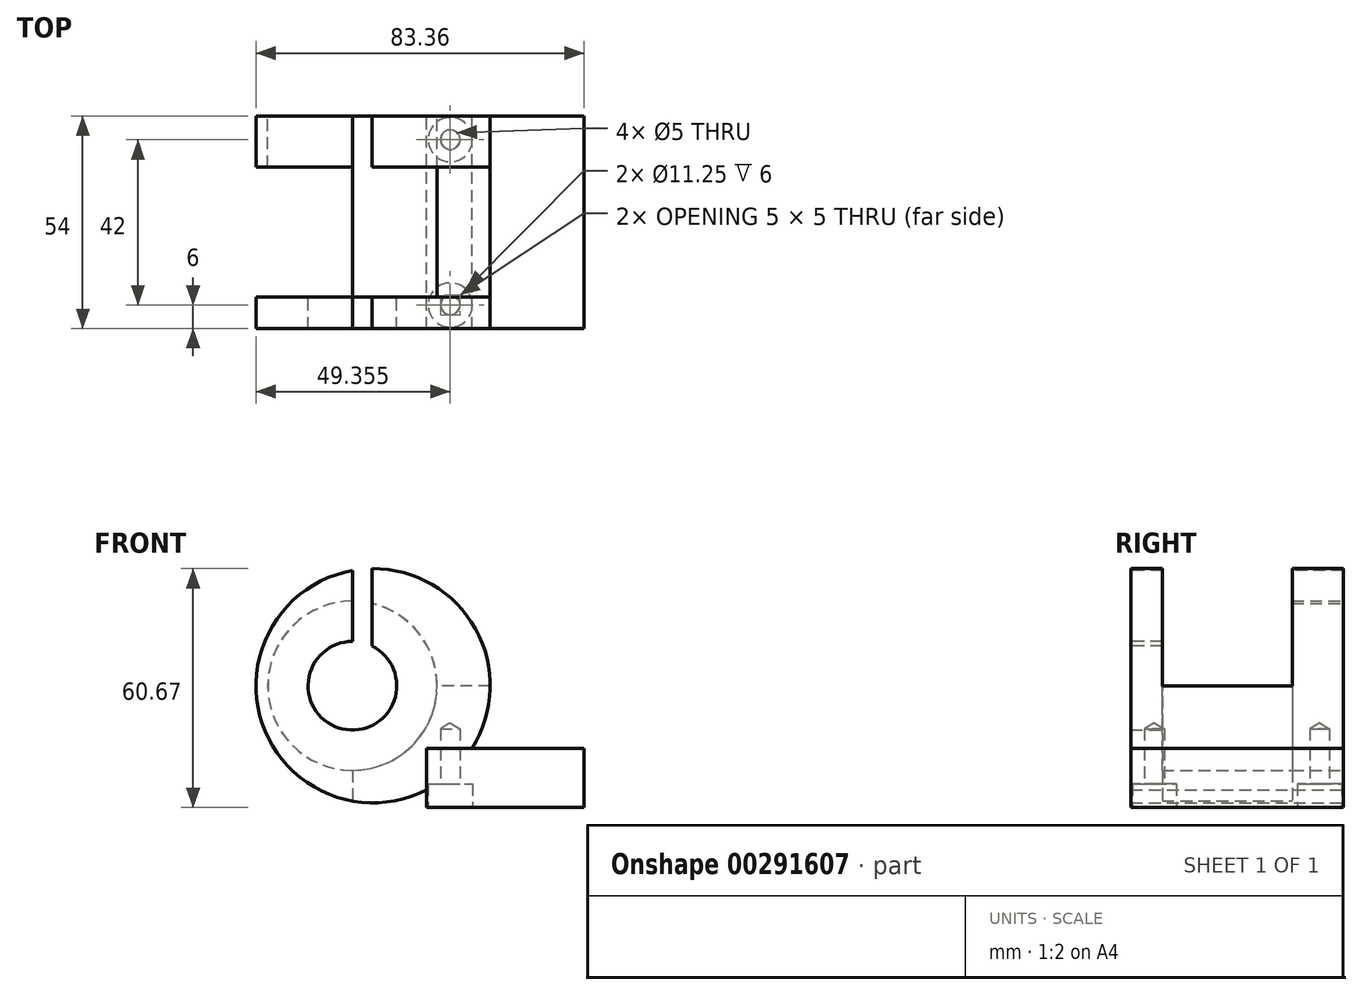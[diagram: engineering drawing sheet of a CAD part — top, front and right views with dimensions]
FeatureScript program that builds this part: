
annotation { "Feature Type Name" : "Feature", "Feature Type Description" : "" }
export const myFeature = defineFeature(function(context is Context, id is Id, definition is map)
    precondition{}
    {
        {
            var Q0;
            Q0=qCreatedBy(makeId("Front.planeOp"),FACE);
            var sketch = newSketch(context, id + "F0", { "sketchPlane" : qUnion([Q0])});
            skCircle(sketch, "E0", {"center": v(0, 0) * mm, "radius": 11.25 * mm});
            skCircle(sketch, "E1", {"center": v(0, 0) * mm, "radius": 21.5 * mm});
            skCircle(sketch, "E2", {"center": v(5.25, 0) * mm, "radius": 29.75 * mm});
            skLineSegment(sketch, "E3.bottom", {"start": v(18.86, -15.92) * mm, "end": v(30.42, -15.87) * mm});
            skLineSegment(sketch, "E3.left", {"start": v(18.86, -15.92) * mm, "end": v(18.86, -26.46) * mm});
            skLineSegment(sketch, "E4.bottom", {"start": v(0, 32.19) * mm, "end": v(5, 32.19) * mm});
            skLineSegment(sketch, "E4.top", {"start": v(0, 7.65) * mm, "end": v(5, 7.65) * mm});
            skLineSegment(sketch, "E4.left", {"start": v(0, 32.19) * mm, "end": v(0, 7.65) * mm});
            skLineSegment(sketch, "E4.right", {"start": v(5, 32.19) * mm, "end": v(5, 7.65) * mm});
            skLineSegment(sketch, "E5.bottom", {"start": v(18.86, -15.92) * mm, "end": v(58.86, -15.92) * mm});
            skLineSegment(sketch, "E5.top", {"start": v(18.86, -30.92) * mm, "end": v(58.86, -30.92) * mm});
            skLineSegment(sketch, "E5.left", {"start": v(18.86, -15.92) * mm, "end": v(18.86, -30.92) * mm});
            skLineSegment(sketch, "E5.right", {"start": v(58.86, -15.92) * mm, "end": v(58.86, -30.92) * mm});
            skCircle(sketch, "E6", {"center": v(17, 0) * mm, "radius": 31.5 * mm, "construction": true});
            skPoint(sketch, "E7", {"position": v(35, 0) * mm});
            skPoint(sketch, "E8", {"position": v(35, -15.92) * mm});
            skPoint(sketch, "E9", {"position": v(5.48, -29.75) * mm});
            skSolve(sketch);
        }
        {
            var Q0;
            Q0=makeQuery(id+"F0.imprint","IMPRINT",FACE,{"disambiguationData":[TD([[makeQuery(id+"F0.imprint","IMPRINT",EDGE,{"derivedFrom":sQuery(id+"F0.wireOp",EDGE,"E1")}),-1.0]])]});
            var Q1;
            {var subQ0=sQuery(id+"F0.wireOp",EDGE,"E3.bottom");Q1=makeQuery(id+"F0.imprint","IMPRINT",FACE,{"disambiguationData":[TD([[makeQuery(id+"F0.imprint","IMPRINT",EDGE,{"derivedFrom":subQ0}),1.0]])]});}
            var Q2;
            {var subQ0=sQuery(id+"F0.wireOp",EDGE,"E4.left");var subQ3=sQuery(id+"F0.wireOp",EDGE,"E1");var subQ4=makeQuery(id+"F0.imprint","INTERSECT",VERTEX,{"derivedFrom":[subQ3,subQ0]});Q2=makeQuery(id+"F0.imprint","IMPRINT",FACE,{"disambiguationData":[TD([[makeQuery(id+"F0.imprint","IMPRINT",EDGE,{"disambiguationData":[TD([[subQ4,-1.0]])],"derivedFrom":subQ3}),-1.0]])]});}
            extrude(context, id + "F1", {"entities" : qUnion([Q0, Q1, Q2]), "depth" : 24.5 * mm, "hasSecondDirection" : true, "secondDirectionOppositeDirection" : true, "secondDirectionDepth" : 29.5 * mm});
        }
        {
            var Q0;
            Q0=makeQuery(id+"F0.imprint","IMPRINT",FACE,{"disambiguationData":[TD([[makeQuery(id+"F0.imprint","IMPRINT",EDGE,{"derivedFrom":sQuery(id+"F0.wireOp",EDGE,"E0")}),-1.0]])]});
            var Q1;
            Q1=makeQuery(id+"F1.opExtrude","CAP_FACE",FACE,{"disambiguationData":[OSD([sQuery(id+"F0.wireOp",EDGE,"E1"),sQuery(id+"F0.wireOp",EDGE,"E2"),sQuery(id+"F0.wireOp",EDGE,"E3.bottom"),sQuery(id+"F0.wireOp",EDGE,"E3.left")])],"isStart":false});
            extrude(context, id + "F2", {"entities" : qUnion([Q0]), "operationType" : NewBodyOperationType.ADD, "endBound" : BoundingType.UP_TO_SURFACE, "endBoundEntityFace" : qUnion([Q1]), "depth" : 35 * mm, "hasSecondDirection" : true, "secondDirectionOppositeDirection" : false, "secondDirectionDepth" : 16.5 * mm});
        }
        {
            var Q0;
            Q0=qCreatedBy(makeId("Top.planeOp"),FACE);
            var sketch = newSketch(context, id + "F3", { "sketchPlane" : qUnion([Q0])});
            skLineSegment(sketch, "E10.bottom", {"start": v(35.86, 16.5) * mm, "end": v(-30.14, 16.5) * mm});
            skLineSegment(sketch, "E10.top", {"start": v(35.86, -16.5) * mm, "end": v(-30.14, -16.5) * mm});
            skLineSegment(sketch, "E10.left", {"start": v(35.86, 16.5) * mm, "end": v(35.86, -16.5) * mm});
            skLineSegment(sketch, "E10.right", {"start": v(-30.14, 16.5) * mm, "end": v(-30.14, -16.5) * mm});
            skPoint(sketch, "E10.middle", {"position": v(2.86, 0) * mm});
            skSolve(sketch);
        }
        {
            var Q0;
            Q0 = qSketchRegion(id + "F3", true);
            extrude(context, id + "F4", {"entities" : qUnion([Q0]), "operationType" : NewBodyOperationType.REMOVE, "depth" : 40 * mm});
        }
        {
            var Q0;
            {var subQ0=sQuery(id+"F0.wireOp",EDGE,"E4.left");var subQ1=sQuery(id+"F0.wireOp",EDGE,"E0");var subQ2=makeQuery(id+"F0.imprint","INTERSECT",VERTEX,{"derivedFrom":[subQ1,subQ0]});Q0=makeQuery(id+"F0.imprint","IMPRINT",FACE,{"disambiguationData":[TD([[makeQuery(id+"F0.imprint","IMPRINT",EDGE,{"disambiguationData":[TD([[subQ2,1.0]])],"derivedFrom":subQ1}),-1.0]])]});}
            var Q1;
            {var subQ0=sQuery(id+"F0.wireOp",EDGE,"E4.left");var subQ1=sQuery(id+"F0.wireOp",EDGE,"E1");var subQ2=makeQuery(id+"F0.imprint","INTERSECT",VERTEX,{"derivedFrom":[subQ1,subQ0]});Q1=makeQuery(id+"F0.imprint","IMPRINT",FACE,{"disambiguationData":[TD([[makeQuery(id+"F0.imprint","IMPRINT",EDGE,{"disambiguationData":[TD([[subQ2,1.0]])],"derivedFrom":subQ1}),-1.0]])]});}
            var Q2;
            Q2=sQuery(id+"F0.wireOp",EDGE,"E4.bottom");
            var Q3;
            Q3=sQuery(id+"F0.wireOp",EDGE,"E4.right");
            var Q4;
            Q4=sQuery(id+"F0.wireOp",EDGE,"E4.left");
            var Q5;
            Q5=sQuery(id+"F0.wireOp",EDGE,"E4.top");
            extrude(context, id + "F5", {"entities" : qUnion([Q0, Q1]), "operationType" : NewBodyOperationType.REMOVE, "surfaceEntities" : qUnion([Q2, Q3, Q4, Q5]), "endBound" : BoundingType.THROUGH_ALL, "oppositeDirection" : true, "depth" : 25 * mm, "hasSecondDirection" : true, "secondDirectionOppositeDirection" : false, "secondDirectionDepth" : 25 * mm});
        }
        {
            var Q0;
            {var subQ1=sQuery(id+"F0.wireOp",EDGE,"E5.top");Q0=makeQuery(id+"F0.imprint","IMPRINT",FACE,{"disambiguationData":[TD([[makeQuery(id+"F0.imprint","IMPRINT",EDGE,{"derivedFrom":subQ1}),1.0]])]});}
            var Q1;
            {var subQ0=sQuery(id+"F0.wireOp",EDGE,"E5.left");var subQ1=sQuery(id+"F0.wireOp",EDGE,"E2");var subQ2=makeQuery(id+"F0.imprint","INTERSECT",VERTEX,{"derivedFrom":[subQ1,subQ0]});Q1=makeQuery(id+"F0.imprint","IMPRINT",FACE,{"disambiguationData":[TD([[makeQuery(id+"F0.imprint","IMPRINT",EDGE,{"disambiguationData":[TD([[subQ2,-1.0]])],"derivedFrom":subQ1}),1.0]])]});}
            extrude(context, id + "F6", {"entities" : qUnion([Q0, Q1]), "depth" : 24.5 * mm, "hasSecondDirection" : true, "secondDirectionOppositeDirection" : true, "secondDirectionDepth" : 29.5 * mm});
        }
        {
            var Q0;
            Q0=makeQuery(id+"F6.opExtrude","SWEPT_FACE",FACE,{"disambiguationData":[OSD([sQuery(id+"F0.wireOp",EDGE,"E5.top")])]});
            var sketch = newSketch(context, id + "F7", { "sketchPlane" : qUnion([Q0])});
            skPoint(sketch, "E11", {"position": v(24.86, 18.5) * mm});
            skPoint(sketch, "E12", {"position": v(24.86, -23.5) * mm});
            skSolve(sketch);
        }
        {
            var Q0;
            Q0=sQuery(id+"F7.wireOp",VERTEX,"E11");
            var Q1;
            Q1=sQuery(id+"F7.wireOp",VERTEX,"E12");
            var Q2;
            Q2=makeQuery(id+"F1.opExtrude","SWEPT_BODY",BODY,{"disambiguationData":[OSD([sQuery(id+"F0.wireOp",EDGE,"E1"),sQuery(id+"F0.wireOp",EDGE,"E2"),sQuery(id+"F0.wireOp",EDGE,"E5.bottom"),sQuery(id+"F0.wireOp",EDGE,"E5.left")])]});
            var Q3;
            Q3=makeQuery(id+"F6.opExtrude","SWEPT_BODY",BODY,{"disambiguationData":[OSD([sQuery(id+"F0.wireOp",EDGE,"E5.bottom"),sQuery(id+"F0.wireOp",EDGE,"E5.top"),sQuery(id+"F0.wireOp",EDGE,"E5.left"),sQuery(id+"F0.wireOp",EDGE,"E5.right")])]});
            hole(context, id + "F8", {"style" : HoleStyle.C_BORE, "endStyle" : HoleEndStyle.BLIND, "standardTappedOrClearance" : lookupTablePath({ "standard" : "ISO", "engagement" : "75%", "pitch" : "1 mm", "size" : "M6", "type" : "Tapped" }), "standardBlindInLast" : lookupTablePath({ "standard" : "ISO", "engagement" : "75%", "pitch" : "1 mm", "size" : "M6", "type" : "Tapped" }), "holeDiameter" : 5 * mm, "cBoreDiameter" : 11.25 * mm, "cBoreDepth" : 6 * mm, "showTappedDepth" : true, "holeDepth" : 20 * mm, "tappedDepth" : 17 * mm, "tapClearance" : 3, "locations" : qUnion([Q0, Q1]), "scope" : qUnion([Q2, Q3]), "majorDiameter" : 6 * mm});
        }
        {
            var Q0;
            Q0=qCreatedBy(makeId("Right.planeOp"),FACE);
            var sketch = newSketch(context, id + "F9", { "sketchPlane" : qUnion([Q0])});
            skLineSegment(sketch, "E13.bottom", {"start": v(-16.5, 31.68) * mm, "end": v(16.5, 31.68) * mm});
            skLineSegment(sketch, "E13.top", {"start": v(-16.5, -31.68) * mm, "end": v(16.5, -31.68) * mm});
            skLineSegment(sketch, "E13.left", {"start": v(-16.5, 31.68) * mm, "end": v(-16.5, -31.68) * mm});
            skLineSegment(sketch, "E13.right", {"start": v(16.5, 31.68) * mm, "end": v(16.5, -31.68) * mm});
            skPoint(sketch, "E13.middle", {"position": v(0, 0) * mm});
            skSolve(sketch);
        }
        {
            var Q0;
            Q0 = qSketchRegion(id + "F9", true);
            extrude(context, id + "F10", {"entities" : qUnion([Q0]), "operationType" : NewBodyOperationType.REMOVE, "oppositeDirection" : true, "depth" : 28.1 * mm});
        }
    });
